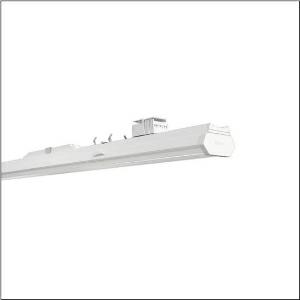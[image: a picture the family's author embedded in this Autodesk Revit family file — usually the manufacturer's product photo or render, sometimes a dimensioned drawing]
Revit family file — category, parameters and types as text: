
# Revit family: licross_r__21_protected_ho_52tp11dn4dxs_9872
name_source: partatom
category: Lighting Fixtures
units: mm (PartAtom-declared; Revit-internal decimal feet)

## family parameters
Cut with Voids When Loaded = No
Host = Face
Light Source = No
Part Type = Normal
Room Calculation Point = No
Round Connector Dimension = Use Diameter
Shared = No

## types (1)
- --- (1 x LED, 13000 lm, 73.1 W, 4000K)
    Apparent Load = 73 VA
    CIE Flux Codes = 84 94 98 99 100
    Color Rendering = 80
    Color Temperature = 4000K
    Default Elevation = 1800 mm
    Description = Licross® 21 Protected HO, luminaire insert, of sheet steel, galvanised, coil coated, white, length: 1.500mm, width: 90mm, height: 103mm, LED rated luminous flux: 13.000lm, light colour: 840, control gear: DALI 2, with plug, 5-pole, with phase selection, mains connection: 220..240V, AC, 50/60Hz, rated input power: 73W, halogen-free wiring, primary light control with lens, of plastic, primary optical cover: cover, of PMMA, light emission: direct distribution, primary light characteristic: symmetric, protection rating (complete): IP64, insulation class (complete): insulation class I (protective earthing), certification: CE, ENEC, VDE, UKCA, protection symbol: D if used in an environment with conductive dust loads with corresponding accessories, impact resistance: IK06, permissible ambient temperature for indoor applications: -25..+40°C, corresponds to IFS (International Featured Standards) requirements for safety and quality in the food industry, reducing of maximum allowable ambient temperature of 5°C with ceiling mounting, LABS conformity tested according to VDMA 24364:2018-05, packaging unit: 1 piece
    Height = 92 mm
    Lamp = 1 x LED
    Lamp Light Flux = 13000 lm
    Lamp Power = 73.1 W
    Lamp count = 1
    Length = 1500 mm
    Luminous efficacy = 178 lm/W
    Manufacturer = Siteco
    ModVariant = No
    Model = 52TP11DN4DXS
    Mounting Place = Ceiling
    Mounting Type = Pendant
    Number of Poles = 1
    OnlyDefault = Yes
    Power Factor = 1
    Product Name = Licross® 21 Protected HO
    Product group = luminaire insert
    ProductGroupID = 902
    Protection Class = Protection class I
    Protection Degree = IP 64
    RLX_Detail_Level = 1
    RLX_Emergency_Light_Flux = 0 lm
    RLX_Emergency_Type = 0
    RLX_Emergency_Type_DB = No
    RlxData = <blob elided: 24257 chars, md5=7a66435b>
    Socket = socket
    Standby Power = 0 W
    System Light Flux = 13000 lm
    System Power = 73 W
    Type Comments = factory setting: luminous flux: 100 % | dim-lin: 254 | 417 mA
    Type Image = l_1256148.jpg
    URL = http://relux.com
    VarID = @adj_128342
    Voltage = 0 V
    Weight = 0.00 kg
    Width = 88 mm

## geometry (parser evidence)
native form markers: Blend x4, Sweep x10
no freeform markers — native parametric forms only
